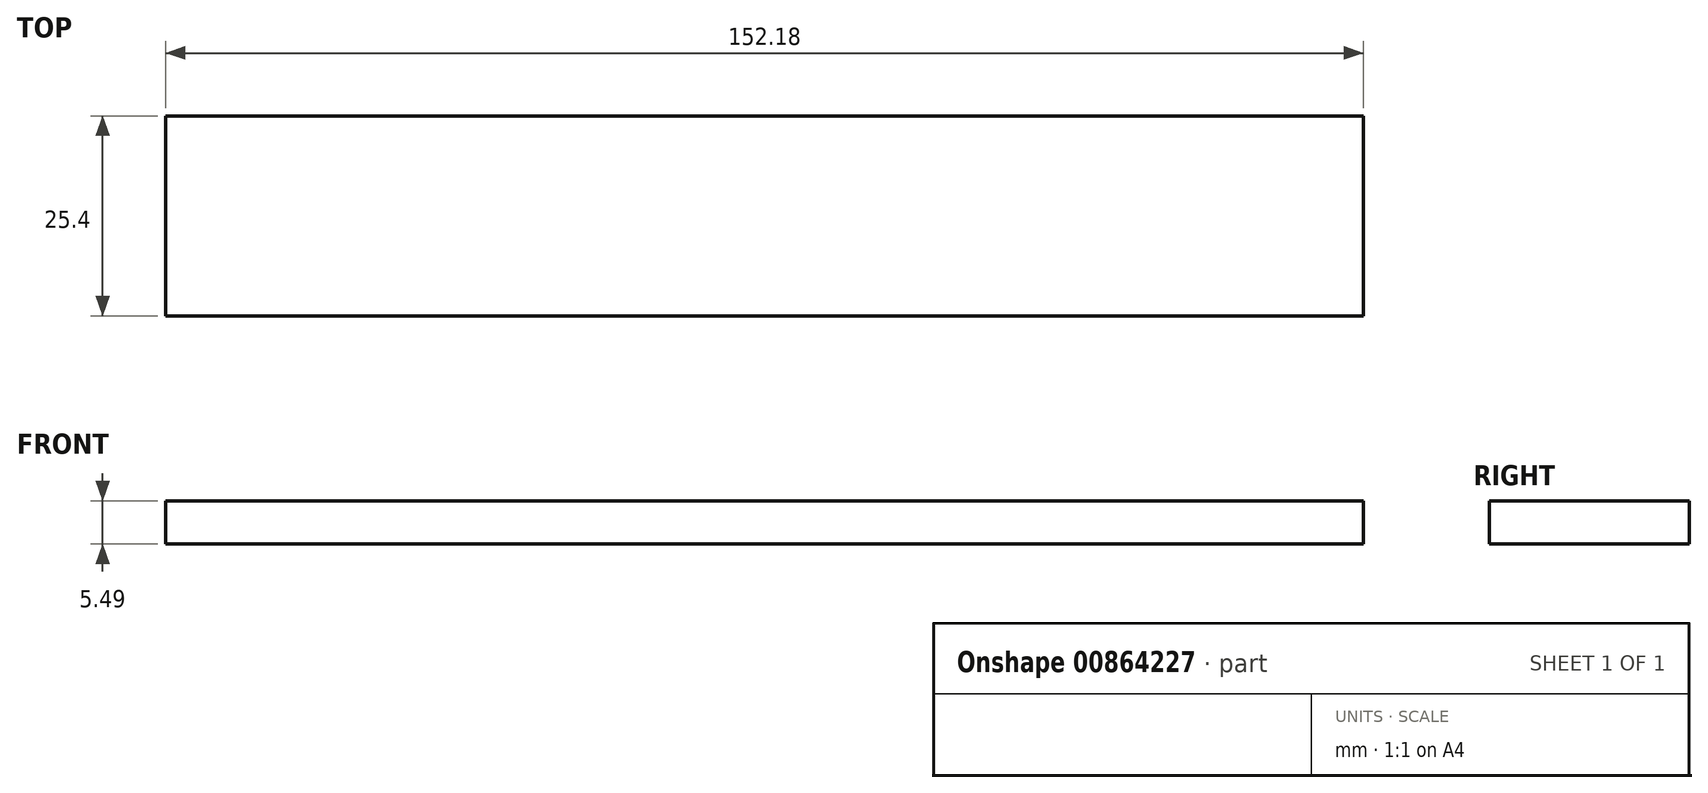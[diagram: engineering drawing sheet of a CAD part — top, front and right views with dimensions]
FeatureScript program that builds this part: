
annotation { "Feature Type Name" : "Feature", "Feature Type Description" : "" }
export const myFeature = defineFeature(function(context is Context, id is Id, definition is map)
    precondition{}
    {
        {
            var Q0;
            Q0=qCreatedBy(makeId("Front.planeOp"),FACE);
            var sketch = newSketch(context, id + "F0", { "sketchPlane" : qUnion([Q0])});
            skLineSegment(sketch, "E0", {"start": v(-76.13, 0) * mm, "end": v(76.05, 0) * mm});
            skLineSegment(sketch, "E1", {"start": v(76.05, 0) * mm, "end": v(76.05, -5.49) * mm});
            skLineSegment(sketch, "E2", {"start": v(76.05, -5.49) * mm, "end": v(-76.13, -5.49) * mm});
            skLineSegment(sketch, "E3", {"start": v(-76.13, -5.49) * mm, "end": v(-76.13, 0) * mm});
            skSolve(sketch);
        }
        {
            var Q0;
            Q0=makeQuery(id+"F0.imprint","IMPRINT",FACE,{"disambiguationData":[TD([[makeQuery(id+"F0.imprint","IMPRINT",EDGE,{"derivedFrom":sQuery(id+"F0.wireOp",EDGE,"E0")}),-1.0]])]});
            extrude(context, id + "F1", {"entities" : qUnion([Q0]), "depth" : 25.4 * mm, "offsetDistance" : 25.4 * mm});
        }
    });
